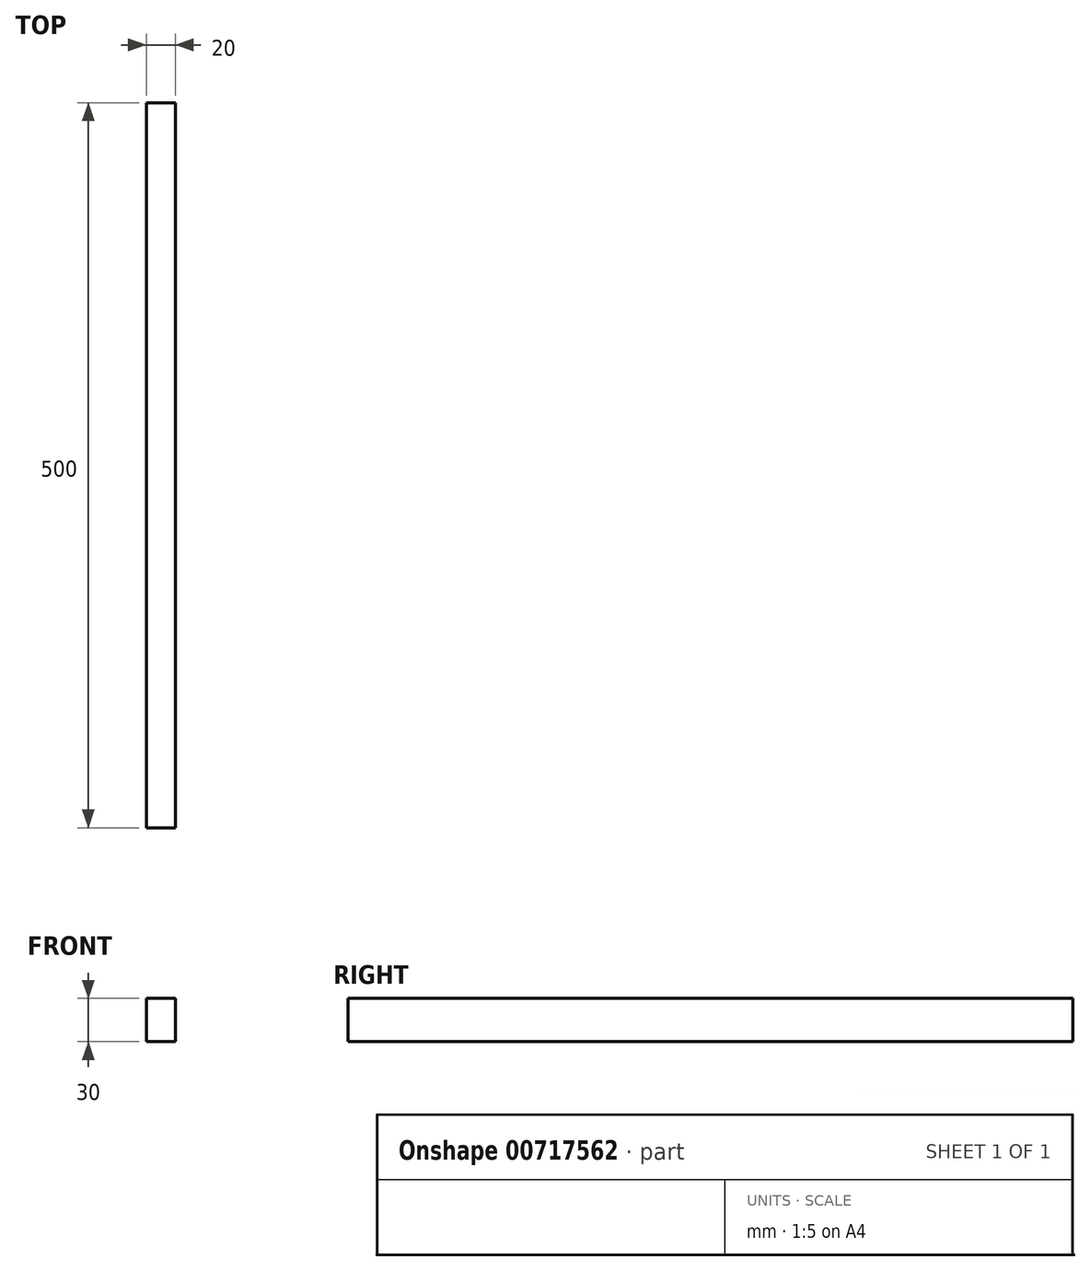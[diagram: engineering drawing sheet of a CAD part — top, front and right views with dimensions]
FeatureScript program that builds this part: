
annotation { "Feature Type Name" : "Feature", "Feature Type Description" : "" }
export const myFeature = defineFeature(function(context is Context, id is Id, definition is map)
    precondition{}
    {
        {
            var Q0;
            Q0=qCreatedBy(makeId("Front.planeOp"),FACE);
            var sketch = newSketch(context, id + "F0", { "sketchPlane" : qUnion([Q0])});
            skLineSegment(sketch, "E0.bottom", {"start": v(10, -15) * mm, "end": v(-10, -15) * mm});
            skLineSegment(sketch, "E0.top", {"start": v(10, 15) * mm, "end": v(-10, 15) * mm});
            skLineSegment(sketch, "E0.left", {"start": v(10, -15) * mm, "end": v(10, 15) * mm});
            skLineSegment(sketch, "E0.right", {"start": v(-10, -15) * mm, "end": v(-10, 15) * mm});
            skPoint(sketch, "E0.middle", {"position": v(0, 0) * mm});
            skSolve(sketch);
        }
        {
            var Q0;
            Q0 = qSketchRegion(id + "F0", true);
            extrude(context, id + "F1", {"entities" : qUnion([Q0]), "endBound" : BoundingType.SYMMETRIC, "depth" : 500 * mm, "offsetDistance" : 25 * mm});
        }
    });
